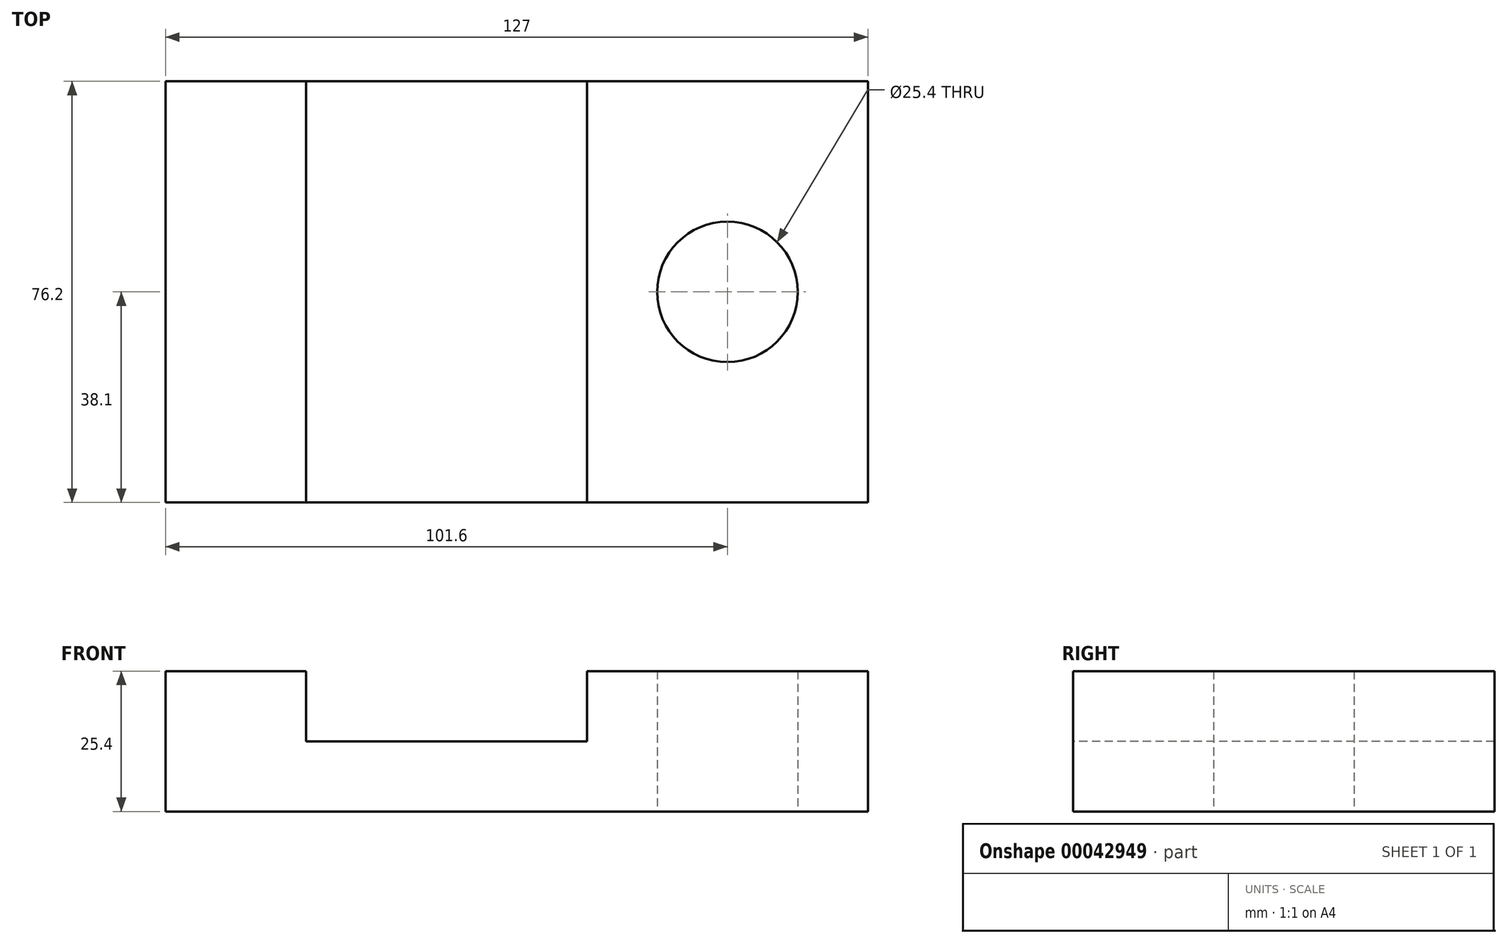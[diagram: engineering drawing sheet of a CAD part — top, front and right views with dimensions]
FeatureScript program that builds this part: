
annotation { "Feature Type Name" : "Feature", "Feature Type Description" : "" }
export const myFeature = defineFeature(function(context is Context, id is Id, definition is map)
    precondition{}
    {
        {
            var Q0;
            Q0=qCreatedBy(makeId("Top.planeOp"),FACE);
            var sketch = newSketch(context, id + "F0", { "sketchPlane" : qUnion([Q0])});
            skLineSegment(sketch, "E0.rect.bottom", {"start": v(63.5, 38.1) * mm, "end": v(-63.5, 38.1) * mm});
            skLineSegment(sketch, "E0.rect.top", {"start": v(63.5, -38.1) * mm, "end": v(-63.5, -38.1) * mm});
            skLineSegment(sketch, "E0.rect.left", {"start": v(63.5, 38.1) * mm, "end": v(63.5, -38.1) * mm});
            skLineSegment(sketch, "E0.rect.right", {"start": v(-63.5, 38.1) * mm, "end": v(-63.5, -38.1) * mm});
            skPoint(sketch, "E0.rect.middle", {"position": v(0, 0) * mm});
            skLineSegment(sketch, "E1", {"start": v(-38.1, 38.1) * mm, "end": v(-38.1, -38.1) * mm});
            skLineSegment(sketch, "E2", {"start": v(12.7, 38.1) * mm, "end": v(12.7, -38.1) * mm});
            skCircle(sketch, "E3", {"center": v(38.1, 0) * mm, "radius": 12.7 * mm});
            skSolve(sketch);
        }
        {
            var Q0;
            {var subQ1=sQuery(id+"F0.wireOp",EDGE,"E0.rect.right");Q0=makeQuery(id+"F0.imprint","IMPRINT",FACE,{"disambiguationData":[TD([[makeQuery(id+"F0.imprint","IMPRINT",EDGE,{"derivedFrom":subQ1}),1.0]])]});}
            extrude(context, id + "F1", {"entities" : qUnion([Q0]), "depth" : 25.4 * mm});
        }
        {
            var Q0;
            {var subQ1=sQuery(id+"F0.wireOp",EDGE,"E1");Q0=makeQuery(id+"F0.imprint","IMPRINT",FACE,{"disambiguationData":[TD([[makeQuery(id+"F0.imprint","IMPRINT",EDGE,{"derivedFrom":subQ1}),1.0]])]});}
            extrude(context, id + "F2", {"entities" : qUnion([Q0]), "operationType" : NewBodyOperationType.ADD, "depth" : 12.7 * mm});
        }
        {
            var Q0;
            {var subQ2=sQuery(id+"F0.wireOp",EDGE,"E0.rect.left");Q0=makeQuery(id+"F0.imprint","IMPRINT",FACE,{"disambiguationData":[TD([[makeQuery(id+"F0.imprint","IMPRINT",EDGE,{"derivedFrom":subQ2}),-1.0]])]});}
            extrude(context, id + "F3", {"entities" : qUnion([Q0]), "operationType" : NewBodyOperationType.ADD, "depth" : 25.4 * mm});
        }
    });
